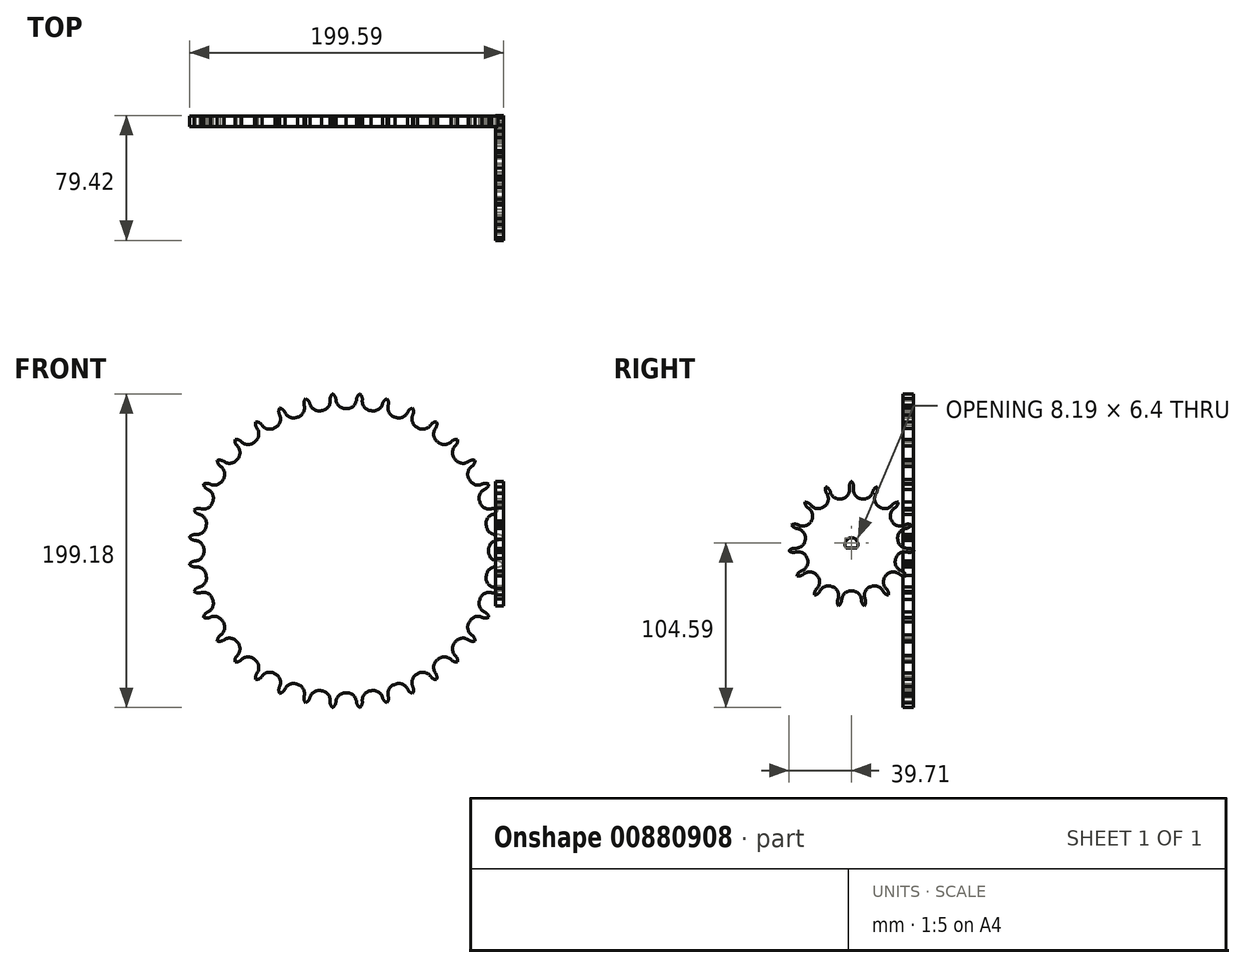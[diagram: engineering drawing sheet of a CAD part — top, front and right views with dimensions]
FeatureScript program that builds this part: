
annotation { "Feature Type Name" : "Feature", "Feature Type Description" : "" }
export const myFeature = defineFeature(function(context is Context, id is Id, definition is map)
    precondition{}
    {
        {
            var Q0;
            Q0=qCreatedBy(makeId("Right.planeOp"),FACE);
            cPlane(context, id + "F0", {"entities" : qUnion([Q0]), "cplaneType" : CPlaneType.OFFSET, "offset" : 95 * mm, "width" : 150 * mm, "height" : 150 * mm});
        }
        {
            var Q0;
            Q0=qCreatedBy(makeId("Front.planeOp"),FACE);
            var sketch = newSketch(context, id + "F1", { "sketchPlane" : qUnion([Q0])});
            skArc(sketch, "E0", {"start": v(-5.07, 74.25) * mm, "mid": v(-3.4, 71.1) * mm, "end": v(0, 70) * mm});
            skArc(sketch, "E1", {"start": v(-5.07, 74.25) * mm, "mid": v(-5.54, 75.94) * mm, "end": v(-6.79, 77.2) * mm});
            skSolve(sketch);
        }
        {
            var Q0;
            Q0=qCreatedBy(makeId("Front.planeOp"),FACE);
            var sketch = newSketch(context, id + "F2", { "sketchPlane" : qUnion([Q0])});
            skArc(sketch, "E2.0", {"start": v(20.63, -71.5) * mm, "mid": v(21.13, -67.97) * mm, "end": v(23.94, -65.78) * mm});
            skArc(sketch, "E2.1", {"start": v(7.9, -74) * mm, "mid": v(9, -70.6) * mm, "end": v(12.16, -68.94) * mm});
            skArc(sketch, "E2.2", {"start": v(51.6, -53.62) * mm, "mid": v(48.3, -52.28) * mm, "end": v(45, -53.62) * mm});
            skArc(sketch, "E2.3", {"start": v(68.04, 30.15) * mm, "mid": v(65.65, 27.5) * mm, "end": v(65.78, 23.94) * mm});
            skArc(sketch, "E2.4", {"start": v(-41.5, -61.77) * mm, "mid": v(-38.49, -59.87) * mm, "end": v(-35, -60.62) * mm});
            skArc(sketch, "E2.5", {"start": v(-17.88, -72.24) * mm, "mid": v(-15.69, -69.43) * mm, "end": v(-12.16, -68.94) * mm});
            skArc(sketch, "E2.6", {"start": v(-72.24, -17.88) * mm, "mid": v(-69.43, -15.69) * mm, "end": v(-68.94, -12.16) * mm});
            skArc(sketch, "E2.7", {"start": v(30.15, 68.04) * mm, "mid": v(27.5, 65.65) * mm, "end": v(23.94, 65.78) * mm});
            skArc(sketch, "E2.8", {"start": v(51.6, 53.62) * mm, "mid": v(48.3, 52.28) * mm, "end": v(45, 53.62) * mm});
            skArc(sketch, "E2.9", {"start": v(-74, 7.9) * mm, "mid": v(-70.6, 9) * mm, "end": v(-68.94, 12.16) * mm});
            skArc(sketch, "E2.10", {"start": v(43.84, -60.13) * mm, "mid": v(43.1, -56.64) * mm, "end": v(45, -53.62) * mm});
            skArc(sketch, "E2.11", {"start": v(32.74, 66.83) * mm, "mid": v(32.6, 63.27) * mm, "end": v(35, 60.62) * mm});
            skArc(sketch, "E2.12", {"start": v(-41.5, 61.77) * mm, "mid": v(-38.49, 59.87) * mm, "end": v(-35, 60.62) * mm});
            skArc(sketch, "E2.13", {"start": v(68.04, -30.15) * mm, "mid": v(65.65, -27.5) * mm, "end": v(65.78, -23.94) * mm});
            skArc(sketch, "E2.14", {"start": v(-61.77, -41.5) * mm, "mid": v(-59.87, -38.49) * mm, "end": v(-60.62, -35) * mm});
            skArc(sketch, "E2.15", {"start": v(-53.62, -51.6) * mm, "mid": v(-52.28, -48.3) * mm, "end": v(-53.62, -45) * mm});
            skArc(sketch, "E2.16", {"start": v(61.77, -41.5) * mm, "mid": v(59.87, -38.49) * mm, "end": v(60.62, -35) * mm});
            skArc(sketch, "E2.17", {"start": v(-43.84, -60.13) * mm, "mid": v(-43.1, -56.64) * mm, "end": v(-45, -53.62) * mm});
            skArc(sketch, "E2.18", {"start": v(-5.07, -74.25) * mm, "mid": v(-3.4, -71.1) * mm, "end": v(0, -70) * mm});
            skArc(sketch, "E2.19", {"start": v(53.62, -51.6) * mm, "mid": v(52.28, -48.3) * mm, "end": v(53.62, -45) * mm});
            skArc(sketch, "E2.20", {"start": v(41.5, 61.77) * mm, "mid": v(38.49, 59.87) * mm, "end": v(35, 60.62) * mm});
            skArc(sketch, "E2.21", {"start": v(53.62, 51.6) * mm, "mid": v(52.28, 48.3) * mm, "end": v(53.62, 45) * mm});
            skArc(sketch, "E2.22", {"start": v(-32.74, 66.83) * mm, "mid": v(-32.6, 63.27) * mm, "end": v(-35, 60.62) * mm});
            skArc(sketch, "E2.23", {"start": v(-60.13, 43.84) * mm, "mid": v(-56.64, 43.1) * mm, "end": v(-53.62, 45) * mm});
            skArc(sketch, "E2.24", {"start": v(17.88, -72.24) * mm, "mid": v(15.69, -69.43) * mm, "end": v(12.16, -68.94) * mm});
            skArc(sketch, "E2.25", {"start": v(60.13, 43.84) * mm, "mid": v(56.64, 43.1) * mm, "end": v(53.62, 45) * mm});
            skArc(sketch, "E2.26", {"start": v(72.24, -17.88) * mm, "mid": v(69.43, -15.69) * mm, "end": v(68.94, -12.16) * mm});
            skArc(sketch, "E2.27", {"start": v(-7.9, -74) * mm, "mid": v(-9, -70.6) * mm, "end": v(-12.16, -68.94) * mm});
            skArc(sketch, "E2.28", {"start": v(-66.83, 32.74) * mm, "mid": v(-63.27, 32.6) * mm, "end": v(-60.62, 35) * mm});
            skArc(sketch, "E2.29", {"start": v(-20.63, -71.5) * mm, "mid": v(-21.13, -67.97) * mm, "end": v(-23.94, -65.78) * mm});
            skArc(sketch, "E2.30", {"start": v(61.77, 41.5) * mm, "mid": v(59.87, 38.49) * mm, "end": v(60.62, 35) * mm});
            skArc(sketch, "E2.31", {"start": v(74.25, -5.07) * mm, "mid": v(71.1, -3.4) * mm, "end": v(70, 0) * mm});
            skArc(sketch, "E2.32", {"start": v(-72.24, 17.88) * mm, "mid": v(-69.43, 15.69) * mm, "end": v(-68.94, 12.16) * mm});
            skArc(sketch, "E2.33", {"start": v(-32.74, -66.83) * mm, "mid": v(-32.6, -63.27) * mm, "end": v(-35, -60.62) * mm});
            skArc(sketch, "E2.34", {"start": v(-74, -7.9) * mm, "mid": v(-70.6, -9) * mm, "end": v(-68.94, -12.16) * mm});
            skArc(sketch, "E2.35", {"start": v(-68.04, 30.15) * mm, "mid": v(-65.65, 27.5) * mm, "end": v(-65.78, 23.94) * mm});
            skArc(sketch, "E2.36", {"start": v(71.5, 20.63) * mm, "mid": v(67.97, 21.13) * mm, "end": v(65.78, 23.94) * mm});
            skArc(sketch, "E2.37", {"start": v(-71.5, -20.63) * mm, "mid": v(-67.97, -21.13) * mm, "end": v(-65.78, -23.94) * mm});
            skArc(sketch, "E2.38", {"start": v(60.13, -43.84) * mm, "mid": v(56.64, -43.1) * mm, "end": v(53.62, -45) * mm});
            skArc(sketch, "E2.39", {"start": v(41.5, -61.77) * mm, "mid": v(38.49, -59.87) * mm, "end": v(35, -60.62) * mm});
            skArc(sketch, "E2.40", {"start": v(-61.77, 41.5) * mm, "mid": v(-59.87, 38.49) * mm, "end": v(-60.62, 35) * mm});
            skArc(sketch, "E2.41", {"start": v(43.84, 60.13) * mm, "mid": v(43.1, 56.64) * mm, "end": v(45, 53.62) * mm});
            skArc(sketch, "E2.42", {"start": v(-66.83, -32.74) * mm, "mid": v(-63.27, -32.6) * mm, "end": v(-60.62, -35) * mm});
            skArc(sketch, "E2.43", {"start": v(71.5, -20.63) * mm, "mid": v(67.97, -21.13) * mm, "end": v(65.78, -23.94) * mm});
            skArc(sketch, "E2.44", {"start": v(-51.6, 53.62) * mm, "mid": v(-48.3, 52.28) * mm, "end": v(-45, 53.62) * mm});
            skArc(sketch, "E2.45", {"start": v(-17.88, 72.24) * mm, "mid": v(-15.69, 69.43) * mm, "end": v(-12.16, 68.94) * mm});
            skArc(sketch, "E2.46", {"start": v(72.24, 17.88) * mm, "mid": v(69.43, 15.69) * mm, "end": v(68.94, 12.16) * mm});
            skArc(sketch, "E2.47", {"start": v(66.83, 32.74) * mm, "mid": v(63.27, 32.6) * mm, "end": v(60.62, 35) * mm});
            skArc(sketch, "E2.48", {"start": v(-74.25, -5.07) * mm, "mid": v(-71.1, -3.4) * mm, "end": v(-70, 0) * mm});
            skArc(sketch, "E2.49", {"start": v(5.07, -74.25) * mm, "mid": v(3.4, -71.1) * mm, "end": v(0, -70) * mm});
            skArc(sketch, "E2.50", {"start": v(-30.15, -68.04) * mm, "mid": v(-27.5, -65.65) * mm, "end": v(-23.94, -65.78) * mm});
            skArc(sketch, "E2.51", {"start": v(30.15, -68.04) * mm, "mid": v(27.5, -65.65) * mm, "end": v(23.94, -65.78) * mm});
            skArc(sketch, "E2.52", {"start": v(-20.63, 71.5) * mm, "mid": v(-21.13, 67.97) * mm, "end": v(-23.94, 65.78) * mm});
            skArc(sketch, "E2.53", {"start": v(-53.62, 51.6) * mm, "mid": v(-52.28, 48.3) * mm, "end": v(-53.62, 45) * mm});
            skArc(sketch, "E2.54", {"start": v(-51.6, -53.62) * mm, "mid": v(-48.3, -52.28) * mm, "end": v(-45, -53.62) * mm});
            skArc(sketch, "E2.55", {"start": v(-60.13, -43.84) * mm, "mid": v(-56.64, -43.1) * mm, "end": v(-53.62, -45) * mm});
            skArc(sketch, "E2.56", {"start": v(74, 7.9) * mm, "mid": v(70.6, 9) * mm, "end": v(68.94, 12.16) * mm});
            skArc(sketch, "E2.57", {"start": v(-74.25, 5.07) * mm, "mid": v(-71.1, 3.4) * mm, "end": v(-70, 0) * mm});
            skArc(sketch, "E2.58", {"start": v(74, -7.9) * mm, "mid": v(70.6, -9) * mm, "end": v(68.94, -12.16) * mm});
            skArc(sketch, "E2.59", {"start": v(-43.84, 60.13) * mm, "mid": v(-43.1, 56.64) * mm, "end": v(-45, 53.62) * mm});
            skArc(sketch, "E2.60", {"start": v(-30.15, 68.04) * mm, "mid": v(-27.5, 65.65) * mm, "end": v(-23.94, 65.78) * mm});
            skArc(sketch, "E2.61", {"start": v(-71.5, 20.63) * mm, "mid": v(-67.97, 21.13) * mm, "end": v(-65.78, 23.94) * mm});
            skArc(sketch, "E2.62", {"start": v(32.74, -66.83) * mm, "mid": v(32.6, -63.27) * mm, "end": v(35, -60.62) * mm});
            skArc(sketch, "E2.63", {"start": v(-68.04, -30.15) * mm, "mid": v(-65.65, -27.5) * mm, "end": v(-65.78, -23.94) * mm});
            skArc(sketch, "E2.64", {"start": v(74.25, 5.07) * mm, "mid": v(71.1, 3.4) * mm, "end": v(70, 0) * mm});
            skArc(sketch, "E2.65", {"start": v(66.83, -32.74) * mm, "mid": v(63.27, -32.6) * mm, "end": v(60.62, -35) * mm});
            skArc(sketch, "E3.0", {"start": v(17.88, 72.24) * mm, "mid": v(15.69, 69.43) * mm, "end": v(12.16, 68.94) * mm});
            skArc(sketch, "E3.1", {"start": v(5.07, 74.25) * mm, "mid": v(3.4, 71.1) * mm, "end": v(0, 70) * mm});
            skArc(sketch, "E3.2", {"start": v(-7.9, 74) * mm, "mid": v(-9, 70.6) * mm, "end": v(-12.16, 68.94) * mm});
            skArc(sketch, "E3.3", {"start": v(-5.07, 74.25) * mm, "mid": v(-3.4, 71.1) * mm, "end": v(0, 70) * mm});
            skArc(sketch, "E3.4", {"start": v(7.9, 74) * mm, "mid": v(9, 70.6) * mm, "end": v(12.16, 68.94) * mm});
            skArc(sketch, "E3.6", {"start": v(20.63, 71.5) * mm, "mid": v(21.13, 67.97) * mm, "end": v(23.94, 65.78) * mm});
            skArc(sketch, "E4.0", {"start": v(20.63, 71.5) * mm, "mid": v(20.76, 73.26) * mm, "end": v(20.02, 74.86) * mm});
            skArc(sketch, "E5.0", {"start": v(17.88, 72.24) * mm, "mid": v(18.65, 73.83) * mm, "end": v(20.09, 74.84) * mm});
            skArc(sketch, "E6.0", {"start": v(7.9, 74) * mm, "mid": v(7.73, 75.75) * mm, "end": v(6.72, 77.2) * mm});
            skArc(sketch, "E7.0", {"start": v(5.07, 74.25) * mm, "mid": v(5.54, 75.94) * mm, "end": v(6.79, 77.2) * mm});
            skPoint(sketch, "E8.0", {"position": v(0, 0) * mm});
            skArc(sketch, "E9.0", {"start": v(-5.07, 74.25) * mm, "mid": v(-5.54, 75.94) * mm, "end": v(-6.79, 77.2) * mm});
            skArc(sketch, "E10.0", {"start": v(-7.9, 74) * mm, "mid": v(-7.73, 75.75) * mm, "end": v(-6.72, 77.2) * mm});
            skArc(sketch, "E11.0", {"start": v(-17.88, 72.24) * mm, "mid": v(-18.65, 73.83) * mm, "end": v(-20.09, 74.84) * mm});
            skArc(sketch, "E12.0", {"start": v(-20.63, 71.5) * mm, "mid": v(-20.76, 73.26) * mm, "end": v(-20.02, 74.86) * mm});
            skPoint(sketch, "E13.0", {"position": v(-31.19, 69.46) * mm});
            skArc(sketch, "E14.0", {"start": v(-30.15, 68.04) * mm, "mid": v(-31.18, 69.47) * mm, "end": v(-32.78, 70.21) * mm});
            skArc(sketch, "E15.0", {"start": v(-32.74, 66.83) * mm, "mid": v(-33.17, 68.54) * mm, "end": v(-32.72, 70.24) * mm});
            skArc(sketch, "E16.0", {"start": v(-41.5, 61.77) * mm, "mid": v(-42.77, 63) * mm, "end": v(-44.47, 63.45) * mm});
            skArc(sketch, "E17.0", {"start": v(-43.84, 60.13) * mm, "mid": v(-44.57, 61.74) * mm, "end": v(-44.42, 63.5) * mm});
            skArc(sketch, "E18.0", {"start": v(30.15, 68.04) * mm, "mid": v(31.18, 69.47) * mm, "end": v(32.78, 70.21) * mm});
            skArc(sketch, "E19.0", {"start": v(32.74, 66.83) * mm, "mid": v(33.17, 68.54) * mm, "end": v(32.72, 70.24) * mm});
            skArc(sketch, "E20.0", {"start": v(41.5, 61.77) * mm, "mid": v(42.77, 63) * mm, "end": v(44.47, 63.45) * mm});
            skArc(sketch, "E21.0", {"start": v(43.84, 60.13) * mm, "mid": v(44.57, 61.74) * mm, "end": v(44.42, 63.5) * mm});
            skArc(sketch, "E22.2", {"start": v(-60.13, 43.84) * mm, "mid": v(-61.74, 44.57) * mm, "end": v(-63.5, 44.42) * mm});
            skArc(sketch, "E23.0", {"start": v(-53.62, 51.6) * mm, "mid": v(-54.61, 53.06) * mm, "end": v(-54.77, 54.82) * mm});
            skArc(sketch, "E24.0", {"start": v(-51.6, 53.62) * mm, "mid": v(-53.06, 54.61) * mm, "end": v(-54.82, 54.77) * mm});
            skArc(sketch, "E25.0", {"start": v(-61.77, 41.5) * mm, "mid": v(-63, 42.77) * mm, "end": v(-63.45, 44.47) * mm});
            skArc(sketch, "E25.1", {"start": v(-66.83, 32.74) * mm, "mid": v(-68.54, 33.17) * mm, "end": v(-70.24, 32.72) * mm});
            skArc(sketch, "E25.2", {"start": v(-68.04, 30.15) * mm, "mid": v(-69.47, 31.18) * mm, "end": v(-70.21, 32.78) * mm});
            skArc(sketch, "E26.0", {"start": v(-72.24, -17.88) * mm, "mid": v(-73.83, -18.65) * mm, "end": v(-74.84, -20.09) * mm});
            skArc(sketch, "E26.1", {"start": v(-68.04, -30.15) * mm, "mid": v(-69.47, -31.18) * mm, "end": v(-70.21, -32.78) * mm});
            skArc(sketch, "E26.2", {"start": v(-71.5, -20.63) * mm, "mid": v(-73.26, -20.76) * mm, "end": v(-74.86, -20.02) * mm});
            skArc(sketch, "E26.3", {"start": v(-74, -7.9) * mm, "mid": v(-75.75, -7.73) * mm, "end": v(-77.2, -6.72) * mm});
            skArc(sketch, "E26.4", {"start": v(-71.5, 20.63) * mm, "mid": v(-73.26, 20.76) * mm, "end": v(-74.86, 20.02) * mm});
            skArc(sketch, "E26.5", {"start": v(-74, 7.9) * mm, "mid": v(-75.75, 7.73) * mm, "end": v(-77.2, 6.72) * mm});
            skArc(sketch, "E26.6", {"start": v(-72.24, 17.88) * mm, "mid": v(-73.83, 18.65) * mm, "end": v(-74.84, 20.09) * mm});
            skArc(sketch, "E26.7", {"start": v(-66.83, -32.74) * mm, "mid": v(-68.54, -33.17) * mm, "end": v(-70.24, -32.72) * mm});
            skArc(sketch, "E26.8", {"start": v(-74.25, -5.07) * mm, "mid": v(-75.94, -5.54) * mm, "end": v(-77.2, -6.79) * mm});
            skArc(sketch, "E26.9", {"start": v(-74.25, 5.07) * mm, "mid": v(-75.94, 5.54) * mm, "end": v(-77.2, 6.79) * mm});
            skArc(sketch, "E27.0", {"start": v(-43.84, -60.13) * mm, "mid": v(-44.57, -61.74) * mm, "end": v(-44.42, -63.5) * mm});
            skArc(sketch, "E27.1", {"start": v(30.15, -68.04) * mm, "mid": v(31.18, -69.47) * mm, "end": v(32.78, -70.21) * mm});
            skArc(sketch, "E27.2", {"start": v(5.07, -74.25) * mm, "mid": v(5.54, -75.94) * mm, "end": v(6.79, -77.2) * mm});
            skArc(sketch, "E27.3", {"start": v(41.5, -61.77) * mm, "mid": v(42.77, -63) * mm, "end": v(44.47, -63.45) * mm});
            skArc(sketch, "E27.4", {"start": v(43.84, -60.13) * mm, "mid": v(44.57, -61.74) * mm, "end": v(44.42, -63.5) * mm});
            skArc(sketch, "E27.5", {"start": v(-30.15, -68.04) * mm, "mid": v(-31.18, -69.47) * mm, "end": v(-32.78, -70.21) * mm});
            skArc(sketch, "E27.6", {"start": v(-61.77, -41.5) * mm, "mid": v(-63, -42.77) * mm, "end": v(-63.45, -44.47) * mm});
            skArc(sketch, "E27.7", {"start": v(20.63, -71.5) * mm, "mid": v(20.76, -73.26) * mm, "end": v(20.02, -74.86) * mm});
            skArc(sketch, "E27.8", {"start": v(-51.6, -53.62) * mm, "mid": v(-53.06, -54.61) * mm, "end": v(-54.82, -54.77) * mm});
            skArc(sketch, "E27.9", {"start": v(51.6, -53.62) * mm, "mid": v(53.06, -54.61) * mm, "end": v(54.82, -54.77) * mm});
            skArc(sketch, "E27.10", {"start": v(-41.5, -61.77) * mm, "mid": v(-42.77, -63) * mm, "end": v(-44.47, -63.45) * mm});
            skArc(sketch, "E27.11", {"start": v(7.9, -74) * mm, "mid": v(7.73, -75.75) * mm, "end": v(6.72, -77.2) * mm});
            skArc(sketch, "E27.12", {"start": v(53.62, -51.6) * mm, "mid": v(54.61, -53.06) * mm, "end": v(54.77, -54.82) * mm});
            skArc(sketch, "E27.13", {"start": v(17.88, -72.24) * mm, "mid": v(18.65, -73.83) * mm, "end": v(20.09, -74.84) * mm});
            skArc(sketch, "E27.14", {"start": v(-17.88, -72.24) * mm, "mid": v(-18.65, -73.83) * mm, "end": v(-20.09, -74.84) * mm});
            skArc(sketch, "E27.15", {"start": v(32.74, -66.83) * mm, "mid": v(33.17, -68.54) * mm, "end": v(32.72, -70.24) * mm});
            skArc(sketch, "E27.16", {"start": v(-7.9, -74) * mm, "mid": v(-7.73, -75.75) * mm, "end": v(-6.72, -77.2) * mm});
            skArc(sketch, "E27.17", {"start": v(61.77, -41.5) * mm, "mid": v(63, -42.77) * mm, "end": v(63.45, -44.47) * mm});
            skArc(sketch, "E27.18", {"start": v(60.13, -43.84) * mm, "mid": v(61.74, -44.57) * mm, "end": v(63.5, -44.42) * mm});
            skArc(sketch, "E27.19", {"start": v(-5.07, -74.25) * mm, "mid": v(-5.54, -75.94) * mm, "end": v(-6.79, -77.2) * mm});
            skArc(sketch, "E27.20", {"start": v(-32.74, -66.83) * mm, "mid": v(-33.17, -68.54) * mm, "end": v(-32.72, -70.24) * mm});
            skArc(sketch, "E27.21", {"start": v(-53.62, -51.6) * mm, "mid": v(-54.61, -53.06) * mm, "end": v(-54.77, -54.82) * mm});
            skArc(sketch, "E27.22", {"start": v(-60.13, -43.84) * mm, "mid": v(-61.74, -44.57) * mm, "end": v(-63.5, -44.42) * mm});
            skArc(sketch, "E27.23", {"start": v(-20.63, -71.5) * mm, "mid": v(-20.76, -73.26) * mm, "end": v(-20.02, -74.86) * mm});
            skArc(sketch, "E28.0", {"start": v(74, -7.9) * mm, "mid": v(75.75, -7.73) * mm, "end": v(77.2, -6.72) * mm});
            skArc(sketch, "E28.1", {"start": v(68.04, -30.15) * mm, "mid": v(69.47, -31.18) * mm, "end": v(70.21, -32.78) * mm});
            skArc(sketch, "E28.2", {"start": v(66.83, 32.74) * mm, "mid": v(68.54, 33.17) * mm, "end": v(70.24, 32.72) * mm});
            skArc(sketch, "E28.3", {"start": v(72.24, -17.88) * mm, "mid": v(73.83, -18.65) * mm, "end": v(74.84, -20.09) * mm});
            skArc(sketch, "E28.4", {"start": v(74, 7.9) * mm, "mid": v(75.75, 7.73) * mm, "end": v(77.2, 6.72) * mm});
            skArc(sketch, "E28.5", {"start": v(71.5, 20.63) * mm, "mid": v(73.26, 20.76) * mm, "end": v(74.86, 20.02) * mm});
            skArc(sketch, "E28.6", {"start": v(71.5, -20.63) * mm, "mid": v(73.26, -20.76) * mm, "end": v(74.86, -20.02) * mm});
            skArc(sketch, "E28.7", {"start": v(74.25, -5.07) * mm, "mid": v(75.94, -5.54) * mm, "end": v(77.2, -6.79) * mm});
            skArc(sketch, "E28.8", {"start": v(66.83, -32.74) * mm, "mid": v(68.54, -33.17) * mm, "end": v(70.24, -32.72) * mm});
            skArc(sketch, "E28.9", {"start": v(74.25, 5.07) * mm, "mid": v(75.94, 5.54) * mm, "end": v(77.2, 6.79) * mm});
            skArc(sketch, "E28.10", {"start": v(68.04, 30.15) * mm, "mid": v(69.47, 31.18) * mm, "end": v(70.21, 32.78) * mm});
            skArc(sketch, "E28.11", {"start": v(72.24, 17.88) * mm, "mid": v(73.83, 18.65) * mm, "end": v(74.84, 20.09) * mm});
            skArc(sketch, "E29.0", {"start": v(51.6, 53.62) * mm, "mid": v(53.06, 54.61) * mm, "end": v(54.82, 54.77) * mm});
            skArc(sketch, "E29.1", {"start": v(53.62, 51.6) * mm, "mid": v(54.61, 53.06) * mm, "end": v(54.77, 54.82) * mm});
            skArc(sketch, "E29.2", {"start": v(78.58, 56.75) * mm, "mid": v(80.19, 57.47) * mm, "end": v(81.94, 57.32) * mm});
            skArc(sketch, "E29.3", {"start": v(61.77, 41.5) * mm, "mid": v(63, 42.77) * mm, "end": v(63.45, 44.47) * mm});
            skArc(sketch, "E29.12", {"start": v(60.13, 43.84) * mm, "mid": v(61.74, 44.57) * mm, "end": v(63.5, 44.42) * mm});
            skSolve(sketch);
        }
        {
            var Q0;
            {var subQ51=sQuery(id+"F2.wireOp",EDGE,"E2.14");Q0=makeQuery(id+"F2.imprint","IMPRINT",FACE,{"disambiguationData":[TD([[makeQuery(id+"F2.imprint","IMPRINT",EDGE,{"derivedFrom":subQ51}),-1.0]])]});}
            extrude(context, id + "F3", {"entities" : qUnion([Q0]), "depth" : 5 * mm, "offsetDistance" : 25 * mm});
        }
        {
            var Q0;
            {var subQ51=sQuery(id+"F2.wireOp",EDGE,"E2.14");Q0=makeQuery(id+"F2.imprint","IMPRINT",FACE,{"disambiguationData":[TD([[makeQuery(id+"F2.imprint","IMPRINT",EDGE,{"derivedFrom":subQ51}),-1.0]])]});}
            extrude(context, id + "F4", {"entities" : qUnion([Q0]), "operationType" : NewBodyOperationType.ADD, "depth" : 3.87 * mm, "offsetDistance" : 25 * mm});
        }
        {
            var Q0;
            Q0=makeQuery(id+"F3.opExtrude","SWEPT_BODY",BODY,{"disambiguationData":[OSD([sQuery(id+"F2.wireOp",EDGE,"E2.14"),sQuery(id+"F2.wireOp",EDGE,"E2.16"),sQuery(id+"F2.wireOp",EDGE,"E2.42"),sQuery(id+"F2.wireOp",EDGE,"E2.60"),sQuery(id+"F2.wireOp",EDGE,"E2.63"),sQuery(id+"F2.wireOp",EDGE,"E3.0"),sQuery(id+"F2.wireOp",EDGE,"E3.1"),sQuery(id+"F2.wireOp",EDGE,"E3.2"),sQuery(id+"F2.wireOp",EDGE,"E3.3"),sQuery(id+"F2.wireOp",EDGE,"E3.4"),sQuery(id+"F2.wireOp",EDGE,"E3.6"),sQuery(id+"F2.wireOp",EDGE,"E2.7"),sQuery(id+"F2.wireOp",EDGE,"E2.12"),sQuery(id+"F2.wireOp",EDGE,"E2.20"),sQuery(id+"F2.wireOp",EDGE,"E2.22"),sQuery(id+"F2.wireOp",EDGE,"E2.25"),sQuery(id+"F2.wireOp",EDGE,"E2.26"),sQuery(id+"F2.wireOp",EDGE,"E2.32"),sQuery(id+"F2.wireOp",EDGE,"E2.35"),sQuery(id+"F2.wireOp",EDGE,"E2.41"),sQuery(id+"F2.wireOp",EDGE,"E2.44"),sQuery(id+"F2.wireOp",EDGE,"E2.45"),sQuery(id+"F2.wireOp",EDGE,"E2.48"),sQuery(id+"F2.wireOp",EDGE,"E2.52"),sQuery(id+"F2.wireOp",EDGE,"E2.59"),sQuery(id+"F2.wireOp",EDGE,"E2.64"),sQuery(id+"F2.wireOp",EDGE,"E4.0"),sQuery(id+"F2.wireOp",EDGE,"E5.0"),sQuery(id+"F2.wireOp",EDGE,"E6.0"),sQuery(id+"F2.wireOp",EDGE,"E7.0"),sQuery(id+"F2.wireOp",EDGE,"E9.0"),sQuery(id+"F2.wireOp",EDGE,"E10.0"),sQuery(id+"F2.wireOp",EDGE,"E11.0"),sQuery(id+"F2.wireOp",EDGE,"E12.0"),sQuery(id+"F2.wireOp",EDGE,"E14.0"),sQuery(id+"F2.wireOp",EDGE,"E15.0"),sQuery(id+"F2.wireOp",EDGE,"E16.0"),sQuery(id+"F2.wireOp",EDGE,"E17.0"),sQuery(id+"F2.wireOp",EDGE,"E18.0"),sQuery(id+"F2.wireOp",EDGE,"E19.0"),sQuery(id+"F2.wireOp",EDGE,"E2.23"),sQuery(id+"F2.wireOp",EDGE,"E2.53"),sQuery(id+"F2.wireOp",EDGE,"E24.0"),sQuery(id+"F2.wireOp",EDGE,"E23.0"),sQuery(id+"F2.wireOp",EDGE,"E25.0"),sQuery(id+"F2.wireOp",EDGE,"E25.1"),sQuery(id+"F2.wireOp",EDGE,"E25.2"),sQuery(id+"F2.wireOp",EDGE,"E2.28"),sQuery(id+"F2.wireOp",EDGE,"E2.40"),sQuery(id+"F2.wireOp",EDGE,"E22.2"),sQuery(id+"F2.wireOp",EDGE,"E26.0"),sQuery(id+"F2.wireOp",EDGE,"E26.1"),sQuery(id+"F2.wireOp",EDGE,"E26.2"),sQuery(id+"F2.wireOp",EDGE,"E26.3"),sQuery(id+"F2.wireOp",EDGE,"E26.4"),sQuery(id+"F2.wireOp",EDGE,"E26.5"),sQuery(id+"F2.wireOp",EDGE,"E26.6"),sQuery(id+"F2.wireOp",EDGE,"E26.7"),sQuery(id+"F2.wireOp",EDGE,"E26.8"),sQuery(id+"F2.wireOp",EDGE,"E26.9"),sQuery(id+"F2.wireOp",EDGE,"E2.6"),sQuery(id+"F2.wireOp",EDGE,"E2.9"),sQuery(id+"F2.wireOp",EDGE,"E2.34"),sQuery(id+"F2.wireOp",EDGE,"E2.37"),sQuery(id+"F2.wireOp",EDGE,"E2.57"),sQuery(id+"F2.wireOp",EDGE,"E2.61"),sQuery(id+"F2.wireOp",EDGE,"E27.0"),sQuery(id+"F2.wireOp",EDGE,"E27.1"),sQuery(id+"F2.wireOp",EDGE,"E27.2"),sQuery(id+"F2.wireOp",EDGE,"E27.3"),sQuery(id+"F2.wireOp",EDGE,"E27.4"),sQuery(id+"F2.wireOp",EDGE,"E27.5"),sQuery(id+"F2.wireOp",EDGE,"E27.6"),sQuery(id+"F2.wireOp",EDGE,"E27.7"),sQuery(id+"F2.wireOp",EDGE,"E27.8"),sQuery(id+"F2.wireOp",EDGE,"E27.9"),sQuery(id+"F2.wireOp",EDGE,"E27.10"),sQuery(id+"F2.wireOp",EDGE,"E27.11"),sQuery(id+"F2.wireOp",EDGE,"E27.12"),sQuery(id+"F2.wireOp",EDGE,"E27.13"),sQuery(id+"F2.wireOp",EDGE,"E27.14"),sQuery(id+"F2.wireOp",EDGE,"E27.15"),sQuery(id+"F2.wireOp",EDGE,"E27.16"),sQuery(id+"F2.wireOp",EDGE,"E27.17"),sQuery(id+"F2.wireOp",EDGE,"E27.18"),sQuery(id+"F2.wireOp",EDGE,"E27.19"),sQuery(id+"F2.wireOp",EDGE,"E27.20"),sQuery(id+"F2.wireOp",EDGE,"E27.21"),sQuery(id+"F2.wireOp",EDGE,"E27.22"),sQuery(id+"F2.wireOp",EDGE,"E27.23"),sQuery(id+"F2.wireOp",EDGE,"E2.0"),sQuery(id+"F2.wireOp",EDGE,"E2.1"),sQuery(id+"F2.wireOp",EDGE,"E2.2"),sQuery(id+"F2.wireOp",EDGE,"E2.4"),sQuery(id+"F2.wireOp",EDGE,"E2.5"),sQuery(id+"F2.wireOp",EDGE,"E2.10"),sQuery(id+"F2.wireOp",EDGE,"E2.15"),sQuery(id+"F2.wireOp",EDGE,"E2.17"),sQuery(id+"F2.wireOp",EDGE,"E2.18"),sQuery(id+"F2.wireOp",EDGE,"E2.19"),sQuery(id+"F2.wireOp",EDGE,"E2.24"),sQuery(id+"F2.wireOp",EDGE,"E2.27"),sQuery(id+"F2.wireOp",EDGE,"E2.29"),sQuery(id+"F2.wireOp",EDGE,"E2.33"),sQuery(id+"F2.wireOp",EDGE,"E2.38"),sQuery(id+"F2.wireOp",EDGE,"E2.39"),sQuery(id+"F2.wireOp",EDGE,"E2.49"),sQuery(id+"F2.wireOp",EDGE,"E2.50"),sQuery(id+"F2.wireOp",EDGE,"E2.51"),sQuery(id+"F2.wireOp",EDGE,"E2.54"),sQuery(id+"F2.wireOp",EDGE,"E2.55"),sQuery(id+"F2.wireOp",EDGE,"E2.62"),sQuery(id+"F2.wireOp",EDGE,"E28.0"),sQuery(id+"F2.wireOp",EDGE,"E28.1"),sQuery(id+"F2.wireOp",EDGE,"E28.3"),sQuery(id+"F2.wireOp",EDGE,"E28.4"),sQuery(id+"F2.wireOp",EDGE,"E28.5"),sQuery(id+"F2.wireOp",EDGE,"E28.6"),sQuery(id+"F2.wireOp",EDGE,"E28.7"),sQuery(id+"F2.wireOp",EDGE,"E28.8"),sQuery(id+"F2.wireOp",EDGE,"E28.9"),sQuery(id+"F2.wireOp",EDGE,"E28.11"),sQuery(id+"F2.wireOp",EDGE,"E2.3"),sQuery(id+"F2.wireOp",EDGE,"E2.13"),sQuery(id+"F2.wireOp",EDGE,"E2.31"),sQuery(id+"F2.wireOp",EDGE,"E2.36"),sQuery(id+"F2.wireOp",EDGE,"E2.43"),sQuery(id+"F2.wireOp",EDGE,"E2.46"),sQuery(id+"F2.wireOp",EDGE,"E2.56"),sQuery(id+"F2.wireOp",EDGE,"E2.58"),sQuery(id+"F2.wireOp",EDGE,"E2.65"),sQuery(id+"F2.wireOp",EDGE,"E29.0"),sQuery(id+"F2.wireOp",EDGE,"E29.1"),sQuery(id+"F2.wireOp",EDGE,"E29.3"),sQuery(id+"F2.wireOp",EDGE,"E2.8"),sQuery(id+"F2.wireOp",EDGE,"E2.11"),sQuery(id+"F2.wireOp",EDGE,"E2.21"),sQuery(id+"F2.wireOp",EDGE,"E28.2"),sQuery(id+"F2.wireOp",EDGE,"E21.0"),sQuery(id+"F2.wireOp",EDGE,"E2.30"),sQuery(id+"F2.wireOp",EDGE,"E20.0"),sQuery(id+"F2.wireOp",EDGE,"E28.10"),sQuery(id+"F2.wireOp",EDGE,"E29.12"),sQuery(id+"F2.wireOp",EDGE,"E2.47")])]});
            var Q1;
            Q1=sQuery(id+"F2.wireOp",VERTEX,"E8.0");
            transform(context, id + "F5", {"entities" : qUnion([Q0]), "transformType" : TransformType.SCALE_UNIFORMLY, "scale" : 1.3, "scalePoint" : qUnion([Q1]), "makeCopy" : false});
        }
        {
            var Q0;
            Q0=qCreatedBy(makeId("Right.planeOp"),FACE);
            var sketch = newSketch(context, id + "F6", { "sketchPlane" : qUnion([Q0])});
            skArc(sketch, "E30", {"start": v(0, 36.48) * mm, "mid": v(1.7, 37.15) * mm, "end": v(2.82, 38.58) * mm});
            skArc(sketch, "E31", {"start": v(4.2, 39.72) * mm, "mid": v(3.26, 39.45) * mm, "end": v(2.82, 38.58) * mm});
            skSolve(sketch);
        }
        {
            var Q0;
            Q0=qCreatedBy(makeId("Front.planeOp"),FACE);
            var sketch = newSketch(context, id + "F7", { "sketchPlane" : qUnion([Q0])});
            skLineSegment(sketch, "E32", {"start": v(46.12, 0) * mm, "end": v(-35.6, 0) * mm});
            skSolve(sketch);
        }
        {
            var Q0;
            {var subQ0=sQuery(id+"FuSN5E2cZiAuNOm_3.wireOp",EDGE,"ce970788-27e3-47bc-be1a-0d92f62c386a.16");var subQ1=makeQuery(id+"FuSN5E2cZiAuNOm_3.imprint","INTERSECT",VERTEX,{"derivedFrom":[sQuery(id+"FuSN5E2cZiAuNOm_3.wireOp",EDGE,"57e1b842-f4a4-4b15-bf3c-e8c0f55d15c8.111"),subQ0]});Q0=makeQuery(id+"FuSN5E2cZiAuNOm_3.imprint","IMPRINT",FACE,{"disambiguationData":[TD([[makeQuery(id+"FuSN5E2cZiAuNOm_3.imprint","IMPRINT",EDGE,{"disambiguationData":[TD([[subQ1,-1.0]])],"derivedFrom":subQ0}),1.0]])]});}
            var sketch = newSketch(context, id + "F8", { "sketchPlane" : qUnion([Q0])});
            skArc(sketch, "E33.0", {"start": v(21.98, -28.21) * mm, "mid": v(20.25, -23.99) * mm, "end": v(21.93, -19.74) * mm});
            skArc(sketch, "E34.0", {"start": v(21.98, -28.21) * mm, "mid": v(23.25, -30.07) * mm, "end": v(23.47, -32.3) * mm});
            skPoint(sketch, "E35.0", {"position": v(29.43, -27) * mm});
            skPoint(sketch, "E36.0", {"position": v(29.92, -26.44) * mm});
            skLineSegment(sketch, "E37", {"start": v(29.43, -27) * mm, "end": v(29.92, -26.44) * mm});
            skLineSegment(sketch, "E38", {"start": v(29.67, -26.72) * mm, "end": v(0, 0) * mm});
            skPoint(sketch, "E39.0", {"position": v(23.77, -32.09) * mm});
            skLineSegment(sketch, "E40", {"start": v(23.17, -32.52) * mm, "end": v(23.77, -32.09) * mm});
            skLineSegment(sketch, "E41", {"start": v(23.47, -32.3) * mm, "end": v(23.98, -33) * mm});
            skArc(sketch, "E42.MirrorCS", {"start": v(30.36, -18.91) * mm, "mid": v(25.97, -17.63) * mm, "end": v(21.93, -19.74) * mm});
            skArc(sketch, "E43.MirrorCS", {"start": v(30.36, -18.91) * mm, "mid": v(32.33, -19.98) * mm, "end": v(34.58, -19.96) * mm});
            skSolve(sketch);
        }
        {
            var Q0;
            Q0=qCreatedBy(id+"F0.planeOp",FACE);
            var sketch = newSketch(context, id + "F9", { "sketchPlane" : qUnion([Q0])});
            skArc(sketch, "E44.0", {"start": v(-33.62, 12.19) * mm, "mid": v(-29.07, 11.85) * mm, "end": v(-25.55, 14.75) * mm});
            skArc(sketch, "E45.0", {"start": v(-27.37, 23.03) * mm, "mid": v(-24.8, 19.25) * mm, "end": v(-25.55, 14.75) * mm});
            skPoint(sketch, "E46.0", {"position": v(-28.99, 24.58) * mm});
            skArc(sketch, "E47.0", {"start": v(-27.37, 23.03) * mm, "mid": v(-29, 24.58) * mm, "end": v(-29.67, 26.72) * mm});
            skArc(sketch, "E48.0", {"start": v(-25.76, 24.8) * mm, "mid": v(-27.47, 26.27) * mm, "end": v(-29.67, 26.72) * mm});
            skArc(sketch, "E49.0", {"start": v(-25.76, 24.8) * mm, "mid": v(-21.74, 22.65) * mm, "end": v(-17.34, 23.87) * mm});
            skArc(sketch, "E50.0", {"start": v(-15.63, 32.17) * mm, "mid": v(-14.82, 27.68) * mm, "end": v(-17.34, 23.87) * mm});
            skArc(sketch, "E51.0", {"start": v(-15.63, 32.17) * mm, "mid": v(-16.5, 34.24) * mm, "end": v(-16.24, 36.48) * mm});
            skPoint(sketch, "E52.0", {"position": v(-14.42, 35.17) * mm});
            skArc(sketch, "E53.0", {"start": v(-13.44, 33.14) * mm, "mid": v(-10.65, 29.53) * mm, "end": v(-6.14, 28.86) * mm});
            skArc(sketch, "E54.0", {"start": v(-1.2, 35.74) * mm, "mid": v(-2.28, 31.31) * mm, "end": v(-6.14, 28.86) * mm});
            skArc(sketch, "E55.0", {"start": v(-1.2, 35.74) * mm, "mid": v(-1.14, 38) * mm, "end": v(0, 39.93) * mm});
            skPoint(sketch, "E56.0", {"position": v(1.13, 37.99) * mm});
            skArc(sketch, "E57.0", {"start": v(-13.44, 33.14) * mm, "mid": v(-14.41, 35.17) * mm, "end": v(-16.24, 36.48) * mm});
            skArc(sketch, "E58.0", {"start": v(1.2, 35.74) * mm, "mid": v(2.28, 31.31) * mm, "end": v(6.14, 28.86) * mm});
            skArc(sketch, "E59.0", {"start": v(1.2, 35.74) * mm, "mid": v(1.14, 38) * mm, "end": v(0, 39.93) * mm});
            skArc(sketch, "E60.0", {"start": v(13.44, 33.14) * mm, "mid": v(10.65, 29.53) * mm, "end": v(6.14, 28.86) * mm});
            skPoint(sketch, "E61.0", {"position": v(14.42, 35.17) * mm});
            skArc(sketch, "E62.0", {"start": v(13.44, 33.14) * mm, "mid": v(14.41, 35.17) * mm, "end": v(16.24, 36.48) * mm});
            skArc(sketch, "E63.0", {"start": v(15.63, 32.17) * mm, "mid": v(16.5, 34.24) * mm, "end": v(16.24, 36.48) * mm});
            skArc(sketch, "E64.0", {"start": v(15.63, 32.17) * mm, "mid": v(14.82, 27.68) * mm, "end": v(17.34, 23.87) * mm});
            skArc(sketch, "E65.0", {"start": v(25.76, 24.8) * mm, "mid": v(21.74, 22.65) * mm, "end": v(17.34, 23.87) * mm});
            skArc(sketch, "E66.0", {"start": v(27.37, 23.03) * mm, "mid": v(29, 24.58) * mm, "end": v(29.67, 26.72) * mm});
            skArc(sketch, "E67.0", {"start": v(27.37, 23.03) * mm, "mid": v(24.8, 19.25) * mm, "end": v(25.55, 14.75) * mm});
            skArc(sketch, "E68.0", {"start": v(33.62, 12.19) * mm, "mid": v(29.07, 11.85) * mm, "end": v(25.55, 14.75) * mm});
            skArc(sketch, "E69.0", {"start": v(25.76, 24.8) * mm, "mid": v(27.47, 26.27) * mm, "end": v(29.67, 26.72) * mm});
            skArc(sketch, "E70.0", {"start": v(33.62, 12.19) * mm, "mid": v(35.78, 12.82) * mm, "end": v(37.97, 12.34) * mm});
            skArc(sketch, "E71.0", {"start": v(34.36, 9.9) * mm, "mid": v(36.48, 10.66) * mm, "end": v(37.97, 12.34) * mm});
            skArc(sketch, "E72.0", {"start": v(34.36, 9.9) * mm, "mid": v(30.48, 7.5) * mm, "end": v(29.35, 3.08) * mm});
            skArc(sketch, "E73.0", {"start": v(-33.62, 12.19) * mm, "mid": v(-35.78, 12.82) * mm, "end": v(-37.97, 12.34) * mm});
            skArc(sketch, "E74.0", {"start": v(-34.36, 9.9) * mm, "mid": v(-36.48, 10.66) * mm, "end": v(-37.97, 12.34) * mm});
            skArc(sketch, "E75.0", {"start": v(-34.36, 9.9) * mm, "mid": v(-30.48, 7.5) * mm, "end": v(-29.35, 3.08) * mm});
            skArc(sketch, "E76.0", {"start": v(-35.67, -2.54) * mm, "mid": v(-31.38, -1) * mm, "end": v(-29.35, 3.08) * mm});
            skPoint(sketch, "E77.0", {"position": v(-37.9, -2.84) * mm});
            skArc(sketch, "E78.0", {"start": v(-35.67, -2.54) * mm, "mid": v(-37.9, -2.84) * mm, "end": v(-39.7, -4.17) * mm});
            skArc(sketch, "E79.0", {"start": v(-35.42, -4.93) * mm, "mid": v(-37.66, -5.1) * mm, "end": v(-39.7, -4.17) * mm});
            skArc(sketch, "E80.0", {"start": v(-35.42, -4.93) * mm, "mid": v(-30.9, -5.54) * mm, "end": v(-28.06, -9.12) * mm});
            skArc(sketch, "E81.0", {"start": v(-31.55, -16.83) * mm, "mid": v(-28.26, -13.68) * mm, "end": v(-28.06, -9.12) * mm});
            skArc(sketch, "E82.0", {"start": v(-31.55, -16.83) * mm, "mid": v(-33.47, -18.01) * mm, "end": v(-34.58, -19.96) * mm});
            skArc(sketch, "E83.0", {"start": v(-30.36, -18.91) * mm, "mid": v(-32.33, -19.98) * mm, "end": v(-34.58, -19.96) * mm});
            skArc(sketch, "E84.0", {"start": v(-30.36, -18.91) * mm, "mid": v(-25.97, -17.63) * mm, "end": v(-21.93, -19.74) * mm});
            skArc(sketch, "E85.0", {"start": v(-21.98, -28.21) * mm, "mid": v(-20.25, -23.99) * mm, "end": v(-21.93, -19.74) * mm});
            skPoint(sketch, "E86.0", {"position": v(-23.25, -30.07) * mm});
            skArc(sketch, "E87.0", {"start": v(-21.98, -28.21) * mm, "mid": v(-23.25, -30.07) * mm, "end": v(-23.47, -32.3) * mm});
            skPoint(sketch, "E88.0", {"position": v(-21.41, -31.4) * mm});
            skArc(sketch, "E89.0", {"start": v(-20.04, -29.62) * mm, "mid": v(-16.56, -26.67) * mm, "end": v(-12, -26.96) * mm});
            skArc(sketch, "E90.0", {"start": v(-20.04, -29.62) * mm, "mid": v(-21.4, -31.4) * mm, "end": v(-23.47, -32.3) * mm});
            skArc(sketch, "E91.0", {"start": v(-8.6, -34.71) * mm, "mid": v(-8.74, -30.15) * mm, "end": v(-12, -26.96) * mm});
            skArc(sketch, "E92.0", {"start": v(-8.6, -34.71) * mm, "mid": v(-9.01, -36.92) * mm, "end": v(-8.3, -39.06) * mm});
            skArc(sketch, "E93.0", {"start": v(-6.26, -35.21) * mm, "mid": v(-6.79, -37.4) * mm, "end": v(-8.3, -39.06) * mm});
            skArc(sketch, "E94.0", {"start": v(-6.26, -35.21) * mm, "mid": v(-4.28, -31.1) * mm, "end": v(0, -29.5) * mm});
            skArc(sketch, "E95.0", {"start": v(6.26, -35.21) * mm, "mid": v(4.28, -31.1) * mm, "end": v(0, -29.5) * mm});
            skArc(sketch, "E96.0", {"start": v(6.26, -35.21) * mm, "mid": v(6.79, -37.4) * mm, "end": v(8.3, -39.06) * mm});
            skArc(sketch, "E97.0", {"start": v(8.6, -34.71) * mm, "mid": v(9.01, -36.92) * mm, "end": v(8.3, -39.06) * mm});
            skArc(sketch, "E98.0", {"start": v(8.6, -34.71) * mm, "mid": v(8.74, -30.15) * mm, "end": v(12, -26.96) * mm});
            skArc(sketch, "E99.0", {"start": v(20.04, -29.62) * mm, "mid": v(16.56, -26.67) * mm, "end": v(12, -26.96) * mm});
            skArc(sketch, "E100.0", {"start": v(20.04, -29.62) * mm, "mid": v(21.4, -31.4) * mm, "end": v(23.47, -32.3) * mm});
            skArc(sketch, "E101.0", {"start": v(21.98, -28.21) * mm, "mid": v(23.25, -30.07) * mm, "end": v(23.47, -32.3) * mm});
            skArc(sketch, "E102.0", {"start": v(21.98, -28.21) * mm, "mid": v(20.25, -23.99) * mm, "end": v(21.93, -19.74) * mm});
            skArc(sketch, "E103.0", {"start": v(30.36, -18.91) * mm, "mid": v(25.97, -17.63) * mm, "end": v(21.93, -19.74) * mm});
            skArc(sketch, "E104.0", {"start": v(30.36, -18.91) * mm, "mid": v(32.33, -19.98) * mm, "end": v(34.58, -19.96) * mm});
            skArc(sketch, "E105.0", {"start": v(31.55, -16.83) * mm, "mid": v(33.47, -18.01) * mm, "end": v(34.58, -19.96) * mm});
            skArc(sketch, "E106.0", {"start": v(31.55, -16.83) * mm, "mid": v(28.26, -13.68) * mm, "end": v(28.06, -9.12) * mm});
            skArc(sketch, "E107.0", {"start": v(35.42, -4.93) * mm, "mid": v(30.9, -5.54) * mm, "end": v(28.06, -9.12) * mm});
            skPoint(sketch, "E108.0", {"position": v(37.66, -5.1) * mm});
            skArc(sketch, "E109.0", {"start": v(35.42, -4.93) * mm, "mid": v(37.66, -5.1) * mm, "end": v(39.7, -4.17) * mm});
            skArc(sketch, "E110.0", {"start": v(35.67, -2.54) * mm, "mid": v(37.9, -2.84) * mm, "end": v(39.7, -4.17) * mm});
            skArc(sketch, "E111.0", {"start": v(35.67, -2.54) * mm, "mid": v(31.38, -1) * mm, "end": v(29.35, 3.08) * mm});
            skSolve(sketch);
        }
        {
            var Q0;
            Q0=qSketchRegion(id+"F9",true);
            extrude(context, id + "F10", {"entities" : qUnion([Q0]), "depth" : 5 * mm, "offsetDistance" : 25 * mm});
        }
        {
            var Q0;
            Q0=makeQuery(id+"F10.opExtrude","SWEPT_BODY",BODY,{"disambiguationData":[OSD([sQuery(id+"F9.wireOp",EDGE,"E44.0"),sQuery(id+"F9.wireOp",EDGE,"E45.0"),sQuery(id+"F9.wireOp",EDGE,"E47.0"),sQuery(id+"F9.wireOp",EDGE,"E48.0"),sQuery(id+"F9.wireOp",EDGE,"E49.0"),sQuery(id+"F9.wireOp",EDGE,"E50.0"),sQuery(id+"F9.wireOp",EDGE,"E51.0"),sQuery(id+"F9.wireOp",EDGE,"E53.0"),sQuery(id+"F9.wireOp",EDGE,"E54.0"),sQuery(id+"F9.wireOp",EDGE,"E55.0"),sQuery(id+"F9.wireOp",EDGE,"E57.0"),sQuery(id+"F9.wireOp",EDGE,"E58.0"),sQuery(id+"F9.wireOp",EDGE,"E59.0"),sQuery(id+"F9.wireOp",EDGE,"E60.0"),sQuery(id+"F9.wireOp",EDGE,"E62.0"),sQuery(id+"F9.wireOp",EDGE,"E63.0"),sQuery(id+"F9.wireOp",EDGE,"E64.0"),sQuery(id+"F9.wireOp",EDGE,"E65.0"),sQuery(id+"F9.wireOp",EDGE,"E66.0"),sQuery(id+"F9.wireOp",EDGE,"E67.0"),sQuery(id+"F9.wireOp",EDGE,"E68.0"),sQuery(id+"F9.wireOp",EDGE,"E69.0"),sQuery(id+"F9.wireOp",EDGE,"E70.0"),sQuery(id+"F9.wireOp",EDGE,"E71.0"),sQuery(id+"F9.wireOp",EDGE,"E72.0"),sQuery(id+"F9.wireOp",EDGE,"E73.0"),sQuery(id+"F9.wireOp",EDGE,"E74.0"),sQuery(id+"F9.wireOp",EDGE,"E75.0"),sQuery(id+"F9.wireOp",EDGE,"E76.0"),sQuery(id+"F9.wireOp",EDGE,"E78.0"),sQuery(id+"F9.wireOp",EDGE,"E79.0"),sQuery(id+"F9.wireOp",EDGE,"E80.0"),sQuery(id+"F9.wireOp",EDGE,"E81.0"),sQuery(id+"F9.wireOp",EDGE,"E82.0"),sQuery(id+"F9.wireOp",EDGE,"E83.0"),sQuery(id+"F9.wireOp",EDGE,"E84.0"),sQuery(id+"F9.wireOp",EDGE,"E85.0"),sQuery(id+"F9.wireOp",EDGE,"E87.0"),sQuery(id+"F9.wireOp",EDGE,"E89.0"),sQuery(id+"F9.wireOp",EDGE,"E90.0"),sQuery(id+"F9.wireOp",EDGE,"E91.0"),sQuery(id+"F9.wireOp",EDGE,"E92.0"),sQuery(id+"F9.wireOp",EDGE,"E93.0"),sQuery(id+"F9.wireOp",EDGE,"E94.0"),sQuery(id+"F9.wireOp",EDGE,"E95.0"),sQuery(id+"F9.wireOp",EDGE,"E96.0"),sQuery(id+"F9.wireOp",EDGE,"E97.0"),sQuery(id+"F9.wireOp",EDGE,"E98.0"),sQuery(id+"F9.wireOp",EDGE,"E99.0"),sQuery(id+"F9.wireOp",EDGE,"E100.0"),sQuery(id+"F9.wireOp",EDGE,"E101.0"),sQuery(id+"F9.wireOp",EDGE,"E102.0"),sQuery(id+"F9.wireOp",EDGE,"E103.0"),sQuery(id+"F9.wireOp",EDGE,"E104.0"),sQuery(id+"F9.wireOp",EDGE,"E105.0"),sQuery(id+"F9.wireOp",EDGE,"E106.0"),sQuery(id+"F9.wireOp",EDGE,"E107.0"),sQuery(id+"F9.wireOp",EDGE,"E109.0"),sQuery(id+"F9.wireOp",EDGE,"E110.0"),sQuery(id+"F9.wireOp",EDGE,"E111.0")])]});
            transform(context, id + "F11", {"entities" : qUnion([Q0]), "transformType" : TransformType.TRANSLATION_3D, "dx" : 0 * mm, "dy" : -39.2 * mm, "dz" : 4.1 * mm, "makeCopy" : false});
        }
        {
            var Q0;
            Q0=makeQuery(id+"F10.opExtrude","CAP_FACE",FACE,{"disambiguationData":[OSD([sQuery(id+"F9.wireOp",EDGE,"E44.0"),sQuery(id+"F9.wireOp",EDGE,"E45.0"),sQuery(id+"F9.wireOp",EDGE,"E47.0"),sQuery(id+"F9.wireOp",EDGE,"E48.0"),sQuery(id+"F9.wireOp",EDGE,"E49.0"),sQuery(id+"F9.wireOp",EDGE,"E50.0"),sQuery(id+"F9.wireOp",EDGE,"E51.0"),sQuery(id+"F9.wireOp",EDGE,"E53.0"),sQuery(id+"F9.wireOp",EDGE,"E54.0"),sQuery(id+"F9.wireOp",EDGE,"E55.0"),sQuery(id+"F9.wireOp",EDGE,"E57.0"),sQuery(id+"F9.wireOp",EDGE,"E58.0"),sQuery(id+"F9.wireOp",EDGE,"E59.0"),sQuery(id+"F9.wireOp",EDGE,"E60.0"),sQuery(id+"F9.wireOp",EDGE,"E62.0"),sQuery(id+"F9.wireOp",EDGE,"E63.0"),sQuery(id+"F9.wireOp",EDGE,"E64.0"),sQuery(id+"F9.wireOp",EDGE,"E65.0"),sQuery(id+"F9.wireOp",EDGE,"E66.0"),sQuery(id+"F9.wireOp",EDGE,"E67.0"),sQuery(id+"F9.wireOp",EDGE,"E68.0"),sQuery(id+"F9.wireOp",EDGE,"E69.0"),sQuery(id+"F9.wireOp",EDGE,"E70.0"),sQuery(id+"F9.wireOp",EDGE,"E71.0"),sQuery(id+"F9.wireOp",EDGE,"E72.0"),sQuery(id+"F9.wireOp",EDGE,"E73.0"),sQuery(id+"F9.wireOp",EDGE,"E74.0"),sQuery(id+"F9.wireOp",EDGE,"E75.0"),sQuery(id+"F9.wireOp",EDGE,"E76.0"),sQuery(id+"F9.wireOp",EDGE,"E78.0"),sQuery(id+"F9.wireOp",EDGE,"E79.0"),sQuery(id+"F9.wireOp",EDGE,"E80.0"),sQuery(id+"F9.wireOp",EDGE,"E81.0"),sQuery(id+"F9.wireOp",EDGE,"E82.0"),sQuery(id+"F9.wireOp",EDGE,"E83.0"),sQuery(id+"F9.wireOp",EDGE,"E84.0"),sQuery(id+"F9.wireOp",EDGE,"E85.0"),sQuery(id+"F9.wireOp",EDGE,"E87.0"),sQuery(id+"F9.wireOp",EDGE,"E89.0"),sQuery(id+"F9.wireOp",EDGE,"E90.0"),sQuery(id+"F9.wireOp",EDGE,"E91.0"),sQuery(id+"F9.wireOp",EDGE,"E92.0"),sQuery(id+"F9.wireOp",EDGE,"E93.0"),sQuery(id+"F9.wireOp",EDGE,"E94.0"),sQuery(id+"F9.wireOp",EDGE,"E95.0"),sQuery(id+"F9.wireOp",EDGE,"E96.0"),sQuery(id+"F9.wireOp",EDGE,"E97.0"),sQuery(id+"F9.wireOp",EDGE,"E98.0"),sQuery(id+"F9.wireOp",EDGE,"E99.0"),sQuery(id+"F9.wireOp",EDGE,"E100.0"),sQuery(id+"F9.wireOp",EDGE,"E101.0"),sQuery(id+"F9.wireOp",EDGE,"E102.0"),sQuery(id+"F9.wireOp",EDGE,"E103.0"),sQuery(id+"F9.wireOp",EDGE,"E104.0"),sQuery(id+"F9.wireOp",EDGE,"E105.0"),sQuery(id+"F9.wireOp",EDGE,"E106.0"),sQuery(id+"F9.wireOp",EDGE,"E107.0"),sQuery(id+"F9.wireOp",EDGE,"E109.0"),sQuery(id+"F9.wireOp",EDGE,"E110.0"),sQuery(id+"F9.wireOp",EDGE,"E111.0")])],"isStart":false});
            var sketch = newSketch(context, id + "F12", { "sketchPlane" : qUnion([Q0])});
            skArc(sketch, "E112.0", {"start": v(-72.82, 16.29) * mm, "mid": v(-68.27, 15.95) * mm, "end": v(-64.75, 18.85) * mm});
            skArc(sketch, "E113.0", {"start": v(-66.57, 27.13) * mm, "mid": v(-64, 23.35) * mm, "end": v(-64.75, 18.85) * mm});
            skPoint(sketch, "E114.0", {"position": v(-68.19, 28.68) * mm});
            skArc(sketch, "E115.0", {"start": v(-66.57, 27.13) * mm, "mid": v(-68.2, 28.68) * mm, "end": v(-68.87, 30.82) * mm});
            skArc(sketch, "E116.0", {"start": v(-64.96, 28.9) * mm, "mid": v(-66.67, 30.37) * mm, "end": v(-68.87, 30.82) * mm});
            skArc(sketch, "E117.0", {"start": v(-64.96, 28.9) * mm, "mid": v(-60.94, 26.75) * mm, "end": v(-56.54, 27.97) * mm});
            skArc(sketch, "E118.0", {"start": v(-54.83, 36.27) * mm, "mid": v(-54.02, 31.78) * mm, "end": v(-56.54, 27.97) * mm});
            skArc(sketch, "E119.0", {"start": v(-54.83, 36.27) * mm, "mid": v(-55.7, 38.34) * mm, "end": v(-55.44, 40.58) * mm});
            skPoint(sketch, "E120.0", {"position": v(-53.62, 39.27) * mm});
            skArc(sketch, "E121.0", {"start": v(-52.64, 37.24) * mm, "mid": v(-49.85, 33.63) * mm, "end": v(-45.34, 32.96) * mm});
            skArc(sketch, "E122.0", {"start": v(-40.4, 39.84) * mm, "mid": v(-41.48, 35.41) * mm, "end": v(-45.34, 32.96) * mm});
            skArc(sketch, "E123.0", {"start": v(-40.4, 39.84) * mm, "mid": v(-40.34, 42.1) * mm, "end": v(-39.2, 44.03) * mm});
            skPoint(sketch, "E124.0", {"position": v(-38.07, 42.09) * mm});
            skArc(sketch, "E125.0", {"start": v(-52.64, 37.24) * mm, "mid": v(-53.61, 39.27) * mm, "end": v(-55.44, 40.58) * mm});
            skArc(sketch, "E126.0", {"start": v(-38, 39.84) * mm, "mid": v(-36.92, 35.41) * mm, "end": v(-33.06, 32.96) * mm});
            skArc(sketch, "E127.0", {"start": v(-38, 39.84) * mm, "mid": v(-38.06, 42.1) * mm, "end": v(-39.2, 44.03) * mm});
            skArc(sketch, "E128.0", {"start": v(-25.76, 37.24) * mm, "mid": v(-28.55, 33.63) * mm, "end": v(-33.06, 32.96) * mm});
            skPoint(sketch, "E129.0", {"position": v(-24.78, 39.27) * mm});
            skArc(sketch, "E130.0", {"start": v(-25.76, 37.24) * mm, "mid": v(-24.79, 39.27) * mm, "end": v(-22.96, 40.58) * mm});
            skArc(sketch, "E131.0", {"start": v(-23.57, 36.27) * mm, "mid": v(-22.7, 38.34) * mm, "end": v(-22.96, 40.58) * mm});
            skArc(sketch, "E132.0", {"start": v(-23.57, 36.27) * mm, "mid": v(-24.38, 31.78) * mm, "end": v(-21.86, 27.97) * mm});
            skArc(sketch, "E133.0", {"start": v(-13.44, 28.9) * mm, "mid": v(-17.46, 26.75) * mm, "end": v(-21.86, 27.97) * mm});
            skArc(sketch, "E134.0", {"start": v(-11.83, 27.13) * mm, "mid": v(-10.2, 28.68) * mm, "end": v(-9.53, 30.82) * mm});
            skArc(sketch, "E135.0", {"start": v(-11.83, 27.13) * mm, "mid": v(-14.4, 23.35) * mm, "end": v(-13.65, 18.85) * mm});
            skArc(sketch, "E136.0", {"start": v(-5.58, 16.29) * mm, "mid": v(-10.13, 15.95) * mm, "end": v(-13.65, 18.85) * mm});
            skArc(sketch, "E137.0", {"start": v(-13.44, 28.9) * mm, "mid": v(-11.73, 30.37) * mm, "end": v(-9.53, 30.82) * mm});
            skArc(sketch, "E138.0", {"start": v(-5.58, 16.29) * mm, "mid": v(-3.42, 16.92) * mm, "end": v(-1.23, 16.44) * mm});
            skArc(sketch, "E139.0", {"start": v(-4.84, 14) * mm, "mid": v(-2.72, 14.76) * mm, "end": v(-1.23, 16.44) * mm});
            skArc(sketch, "E140.0", {"start": v(-4.84, 14) * mm, "mid": v(-8.72, 11.6) * mm, "end": v(-9.85, 7.18) * mm});
            skArc(sketch, "E141.0", {"start": v(-72.82, 16.29) * mm, "mid": v(-74.98, 16.92) * mm, "end": v(-77.17, 16.44) * mm});
            skArc(sketch, "E142.0", {"start": v(-73.56, 14) * mm, "mid": v(-75.68, 14.76) * mm, "end": v(-77.17, 16.44) * mm});
            skArc(sketch, "E143.0", {"start": v(-73.56, 14) * mm, "mid": v(-69.68, 11.6) * mm, "end": v(-68.55, 7.18) * mm});
            skArc(sketch, "E144.0", {"start": v(-74.87, 1.56) * mm, "mid": v(-70.58, 3.1) * mm, "end": v(-68.55, 7.18) * mm});
            skPoint(sketch, "E145.0", {"position": v(-77.1, 1.26) * mm});
            skArc(sketch, "E146.0", {"start": v(-74.87, 1.56) * mm, "mid": v(-77.1, 1.26) * mm, "end": v(-78.9, -0.07) * mm});
            skArc(sketch, "E147.0", {"start": v(-74.62, -0.83) * mm, "mid": v(-76.86, -1) * mm, "end": v(-78.9, -0.07) * mm});
            skArc(sketch, "E148.0", {"start": v(-74.62, -0.83) * mm, "mid": v(-70.1, -1.44) * mm, "end": v(-67.26, -5.02) * mm});
            skArc(sketch, "E149.0", {"start": v(-70.75, -12.73) * mm, "mid": v(-67.46, -9.58) * mm, "end": v(-67.26, -5.02) * mm});
            skArc(sketch, "E150.0", {"start": v(-70.75, -12.73) * mm, "mid": v(-72.67, -13.91) * mm, "end": v(-73.78, -15.86) * mm});
            skArc(sketch, "E151.0", {"start": v(-69.56, -14.81) * mm, "mid": v(-71.53, -15.88) * mm, "end": v(-73.78, -15.86) * mm});
            skArc(sketch, "E152.0", {"start": v(-69.56, -14.81) * mm, "mid": v(-65.17, -13.53) * mm, "end": v(-61.13, -15.64) * mm});
            skArc(sketch, "E153.0", {"start": v(-61.18, -24.11) * mm, "mid": v(-59.45, -19.89) * mm, "end": v(-61.13, -15.64) * mm});
            skPoint(sketch, "E154.0", {"position": v(-62.45, -25.97) * mm});
            skArc(sketch, "E155.0", {"start": v(-61.18, -24.11) * mm, "mid": v(-62.45, -25.97) * mm, "end": v(-62.67, -28.2) * mm});
            skPoint(sketch, "E156.0", {"position": v(-60.61, -27.3) * mm});
            skArc(sketch, "E157.0", {"start": v(-59.24, -25.52) * mm, "mid": v(-55.76, -22.57) * mm, "end": v(-51.2, -22.86) * mm});
            skArc(sketch, "E158.0", {"start": v(-59.24, -25.52) * mm, "mid": v(-60.6, -27.3) * mm, "end": v(-62.67, -28.2) * mm});
            skArc(sketch, "E159.0", {"start": v(-47.8, -30.61) * mm, "mid": v(-47.94, -26.05) * mm, "end": v(-51.2, -22.86) * mm});
            skArc(sketch, "E160.0", {"start": v(-47.8, -30.61) * mm, "mid": v(-48.21, -32.82) * mm, "end": v(-47.5, -34.96) * mm});
            skArc(sketch, "E161.0", {"start": v(-45.46, -31.11) * mm, "mid": v(-45.99, -33.3) * mm, "end": v(-47.5, -34.96) * mm});
            skArc(sketch, "E162.0", {"start": v(-45.46, -31.11) * mm, "mid": v(-43.48, -27) * mm, "end": v(-39.2, -25.4) * mm});
            skArc(sketch, "E163.0", {"start": v(-32.94, -31.11) * mm, "mid": v(-34.92, -27) * mm, "end": v(-39.2, -25.4) * mm});
            skArc(sketch, "E164.0", {"start": v(-32.94, -31.11) * mm, "mid": v(-32.41, -33.3) * mm, "end": v(-30.9, -34.96) * mm});
            skArc(sketch, "E165.0", {"start": v(-30.6, -30.61) * mm, "mid": v(-30.19, -32.82) * mm, "end": v(-30.9, -34.96) * mm});
            skArc(sketch, "E166.0", {"start": v(-30.6, -30.61) * mm, "mid": v(-30.46, -26.05) * mm, "end": v(-27.2, -22.86) * mm});
            skArc(sketch, "E167.0", {"start": v(-19.16, -25.52) * mm, "mid": v(-22.64, -22.57) * mm, "end": v(-27.2, -22.86) * mm});
            skArc(sketch, "E168.0", {"start": v(-19.16, -25.52) * mm, "mid": v(-17.8, -27.3) * mm, "end": v(-15.73, -28.2) * mm});
            skArc(sketch, "E169.0", {"start": v(-17.22, -24.11) * mm, "mid": v(-15.95, -25.97) * mm, "end": v(-15.73, -28.2) * mm});
            skArc(sketch, "E170.0", {"start": v(-17.22, -24.11) * mm, "mid": v(-18.95, -19.89) * mm, "end": v(-17.27, -15.64) * mm});
            skArc(sketch, "E171.0", {"start": v(-8.84, -14.81) * mm, "mid": v(-13.23, -13.53) * mm, "end": v(-17.27, -15.64) * mm});
            skArc(sketch, "E172.0", {"start": v(-8.84, -14.81) * mm, "mid": v(-6.87, -15.88) * mm, "end": v(-4.62, -15.86) * mm});
            skArc(sketch, "E173.0", {"start": v(-7.65, -12.73) * mm, "mid": v(-5.73, -13.91) * mm, "end": v(-4.62, -15.86) * mm});
            skArc(sketch, "E174.0", {"start": v(-7.65, -12.73) * mm, "mid": v(-10.94, -9.58) * mm, "end": v(-11.14, -5.02) * mm});
            skArc(sketch, "E175.0", {"start": v(-3.78, -0.83) * mm, "mid": v(-8.3, -1.44) * mm, "end": v(-11.14, -5.02) * mm});
            skPoint(sketch, "E176.0", {"position": v(-1.54, -1) * mm});
            skArc(sketch, "E177.0", {"start": v(-3.78, -0.83) * mm, "mid": v(-1.54, -1) * mm, "end": v(0.5, -0.07) * mm});
            skArc(sketch, "E178.0", {"start": v(-3.53, 1.56) * mm, "mid": v(-1.3, 1.26) * mm, "end": v(0.5, -0.07) * mm});
            skArc(sketch, "E179.0", {"start": v(-3.53, 1.56) * mm, "mid": v(-7.82, 3.1) * mm, "end": v(-9.85, 7.18) * mm});
            skPoint(sketch, "E180.0", {"position": v(-39.2, 4.1) * mm});
            skCircle(sketch, "E181", {"center": v(-39.2, 4.1) * mm, "radius": 3.8 * mm});
            skSolve(sketch);
        }
        {
            var Q0;
            Q0=makeQuery(id+"F12.imprint","IMPRINT",FACE,{"disambiguationData":[TD([[makeQuery(id+"F12.imprint","IMPRINT",EDGE,{"derivedFrom":sQuery(id+"F12.wireOp",EDGE,"E112.0")}),-1.0]])]});
            var sketch = newSketch(context, id + "F13", { "sketchPlane" : qUnion([Q0])});
            skPoint(sketch, "E182.0", {"position": v(-39.2, 4.1) * mm});
            skArc(sketch, "E183", {"start": v(-35.8, 1.8) * mm, "mid": v(-39.2, 8.2) * mm, "end": v(-42.6, 1.8) * mm});
            skLineSegment(sketch, "E184", {"start": v(-39.2, 1.8) * mm, "end": v(-42.6, 1.8) * mm});
            skLineSegment(sketch, "E185", {"start": v(-42.6, 1.8) * mm, "end": v(-35.8, 1.8) * mm});
            skSolve(sketch);
        }
        {
            var Q0;
            Q0 = qSketchRegion(id + "F13", true);
            var Q1;
            Q1=makeQuery(id+"F10.opExtrude","CAP_FACE",FACE,{"disambiguationData":[OSD([sQuery(id+"F9.wireOp",EDGE,"E44.0"),sQuery(id+"F9.wireOp",EDGE,"E45.0"),sQuery(id+"F9.wireOp",EDGE,"E47.0"),sQuery(id+"F9.wireOp",EDGE,"E48.0"),sQuery(id+"F9.wireOp",EDGE,"E49.0"),sQuery(id+"F9.wireOp",EDGE,"E50.0"),sQuery(id+"F9.wireOp",EDGE,"E51.0"),sQuery(id+"F9.wireOp",EDGE,"E53.0"),sQuery(id+"F9.wireOp",EDGE,"E54.0"),sQuery(id+"F9.wireOp",EDGE,"E55.0"),sQuery(id+"F9.wireOp",EDGE,"E57.0"),sQuery(id+"F9.wireOp",EDGE,"E58.0"),sQuery(id+"F9.wireOp",EDGE,"E59.0"),sQuery(id+"F9.wireOp",EDGE,"E60.0"),sQuery(id+"F9.wireOp",EDGE,"E62.0"),sQuery(id+"F9.wireOp",EDGE,"E63.0"),sQuery(id+"F9.wireOp",EDGE,"E64.0"),sQuery(id+"F9.wireOp",EDGE,"E65.0"),sQuery(id+"F9.wireOp",EDGE,"E66.0"),sQuery(id+"F9.wireOp",EDGE,"E67.0"),sQuery(id+"F9.wireOp",EDGE,"E68.0"),sQuery(id+"F9.wireOp",EDGE,"E69.0"),sQuery(id+"F9.wireOp",EDGE,"E70.0"),sQuery(id+"F9.wireOp",EDGE,"E71.0"),sQuery(id+"F9.wireOp",EDGE,"E72.0"),sQuery(id+"F9.wireOp",EDGE,"E73.0"),sQuery(id+"F9.wireOp",EDGE,"E74.0"),sQuery(id+"F9.wireOp",EDGE,"E75.0"),sQuery(id+"F9.wireOp",EDGE,"E76.0"),sQuery(id+"F9.wireOp",EDGE,"E78.0"),sQuery(id+"F9.wireOp",EDGE,"E79.0"),sQuery(id+"F9.wireOp",EDGE,"E80.0"),sQuery(id+"F9.wireOp",EDGE,"E81.0"),sQuery(id+"F9.wireOp",EDGE,"E82.0"),sQuery(id+"F9.wireOp",EDGE,"E83.0"),sQuery(id+"F9.wireOp",EDGE,"E84.0"),sQuery(id+"F9.wireOp",EDGE,"E85.0"),sQuery(id+"F9.wireOp",EDGE,"E87.0"),sQuery(id+"F9.wireOp",EDGE,"E89.0"),sQuery(id+"F9.wireOp",EDGE,"E90.0"),sQuery(id+"F9.wireOp",EDGE,"E91.0"),sQuery(id+"F9.wireOp",EDGE,"E92.0"),sQuery(id+"F9.wireOp",EDGE,"E93.0"),sQuery(id+"F9.wireOp",EDGE,"E94.0"),sQuery(id+"F9.wireOp",EDGE,"E95.0"),sQuery(id+"F9.wireOp",EDGE,"E96.0"),sQuery(id+"F9.wireOp",EDGE,"E97.0"),sQuery(id+"F9.wireOp",EDGE,"E98.0"),sQuery(id+"F9.wireOp",EDGE,"E99.0"),sQuery(id+"F9.wireOp",EDGE,"E100.0"),sQuery(id+"F9.wireOp",EDGE,"E101.0"),sQuery(id+"F9.wireOp",EDGE,"E102.0"),sQuery(id+"F9.wireOp",EDGE,"E103.0"),sQuery(id+"F9.wireOp",EDGE,"E104.0"),sQuery(id+"F9.wireOp",EDGE,"E105.0"),sQuery(id+"F9.wireOp",EDGE,"E106.0"),sQuery(id+"F9.wireOp",EDGE,"E107.0"),sQuery(id+"F9.wireOp",EDGE,"E109.0"),sQuery(id+"F9.wireOp",EDGE,"E110.0"),sQuery(id+"F9.wireOp",EDGE,"E111.0")])],"isStart":true});
            extrude(context, id + "F14", {"entities" : qUnion([Q0]), "operationType" : NewBodyOperationType.REMOVE, "endBound" : BoundingType.UP_TO_SURFACE, "oppositeDirection" : true, "depth" : 25 * mm, "endBoundEntityFace" : qUnion([Q1]), "offsetDistance" : 25 * mm});
        }
    });
